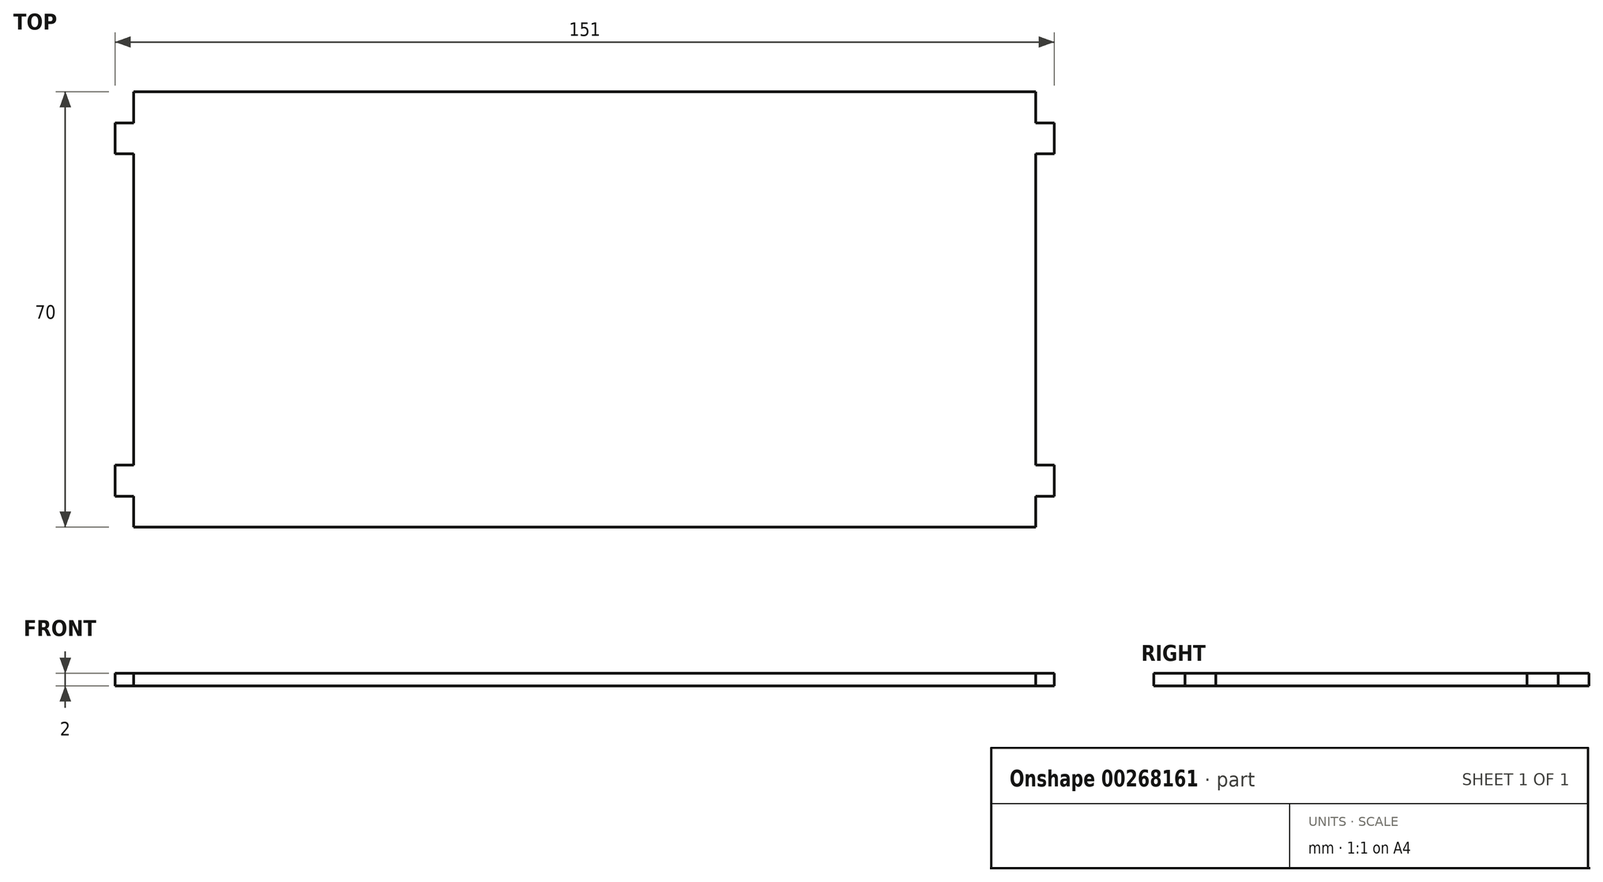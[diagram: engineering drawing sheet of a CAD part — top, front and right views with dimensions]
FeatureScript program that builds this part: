
annotation { "Feature Type Name" : "Feature", "Feature Type Description" : "" }
export const myFeature = defineFeature(function(context is Context, id is Id, definition is map)
    precondition{}
    {
        {
            var Q0;
            Q0=qCreatedBy(makeId("Top.planeOp"),FACE);
            var sketch = newSketch(context, id + "F0", { "sketchPlane" : qUnion([Q0])});
            skLineSegment(sketch, "E0.bottom", {"start": v(-96.7, 21.03) * mm, "end": v(48.3, 21.03) * mm});
            skLineSegment(sketch, "E0.top", {"start": v(-96.7, -48.97) * mm, "end": v(48.3, -48.97) * mm});
            skLineSegment(sketch, "E0.left", {"start": v(-96.7, 21.03) * mm, "end": v(-96.7, -48.97) * mm});
            skLineSegment(sketch, "E0.right", {"start": v(48.3, 21.03) * mm, "end": v(48.3, -48.97) * mm});
            skSolve(sketch);
        }
        {
            var Q0;
            Q0 = qSketchRegion(id + "F0", true);
            extrude(context, id + "F1", {"entities" : qUnion([Q0]), "depth" : 2 * mm});
        }
        {
            var Q0;
            Q0=makeQuery(id+"F1.opExtrude","SWEPT_FACE",FACE,{"disambiguationData":[OSD([sQuery(id+"F0.wireOp",EDGE,"E0.left")])]});
            var sketch = newSketch(context, id + "F2", { "sketchPlane" : qUnion([Q0])});
            skLineSegment(sketch, "E1.bottom", {"start": v(-16.03, 0) * mm, "end": v(-11.03, 0) * mm});
            skLineSegment(sketch, "E1.top", {"start": v(-16.03, 2) * mm, "end": v(-11.03, 2) * mm});
            skLineSegment(sketch, "E1.left", {"start": v(-16.03, 0) * mm, "end": v(-16.03, 2) * mm});
            skLineSegment(sketch, "E1.right", {"start": v(-11.03, 0) * mm, "end": v(-11.03, 2) * mm});
            skLineSegment(sketch, "E2.bottom", {"start": v(38.97, 0) * mm, "end": v(43.97, 0) * mm});
            skLineSegment(sketch, "E2.top", {"start": v(38.97, 2) * mm, "end": v(43.97, 2) * mm});
            skLineSegment(sketch, "E2.left", {"start": v(38.97, 0) * mm, "end": v(38.97, 2) * mm});
            skLineSegment(sketch, "E2.right", {"start": v(43.97, 0) * mm, "end": v(43.97, 2) * mm});
            skSolve(sketch);
        }
        {
            var Q0;
            Q0 = qSketchRegion(id + "F2", true);
            extrude(context, id + "F3", {"entities" : qUnion([Q0]), "operationType" : NewBodyOperationType.ADD, "depth" : 3 * mm});
        }
        {
            var Q0;
            Q0=makeQuery(id+"F1.opExtrude","SWEPT_FACE",FACE,{"disambiguationData":[OSD([sQuery(id+"F0.wireOp",EDGE,"E0.right")])]});
            var sketch = newSketch(context, id + "F4", { "sketchPlane" : qUnion([Q0])});
            skLineSegment(sketch, "E3.bottom", {"start": v(16.03, 2) * mm, "end": v(11.03, 2) * mm});
            skLineSegment(sketch, "E3.top", {"start": v(16.03, 0) * mm, "end": v(11.03, 0) * mm});
            skLineSegment(sketch, "E3.left", {"start": v(16.03, 2) * mm, "end": v(16.03, 0) * mm});
            skLineSegment(sketch, "E3.right", {"start": v(11.03, 2) * mm, "end": v(11.03, 0) * mm});
            skLineSegment(sketch, "E4.bottom", {"start": v(-43.97, 2) * mm, "end": v(-38.97, 2) * mm});
            skLineSegment(sketch, "E4.top", {"start": v(-43.97, 0) * mm, "end": v(-38.97, 0) * mm});
            skLineSegment(sketch, "E4.left", {"start": v(-43.97, 2) * mm, "end": v(-43.97, 0) * mm});
            skLineSegment(sketch, "E4.right", {"start": v(-38.97, 2) * mm, "end": v(-38.97, 0) * mm});
            skSolve(sketch);
        }
        {
            var Q0;
            Q0 = qSketchRegion(id + "F4", true);
            extrude(context, id + "F5", {"entities" : qUnion([Q0]), "operationType" : NewBodyOperationType.ADD, "depth" : 3 * mm});
        }
    });
